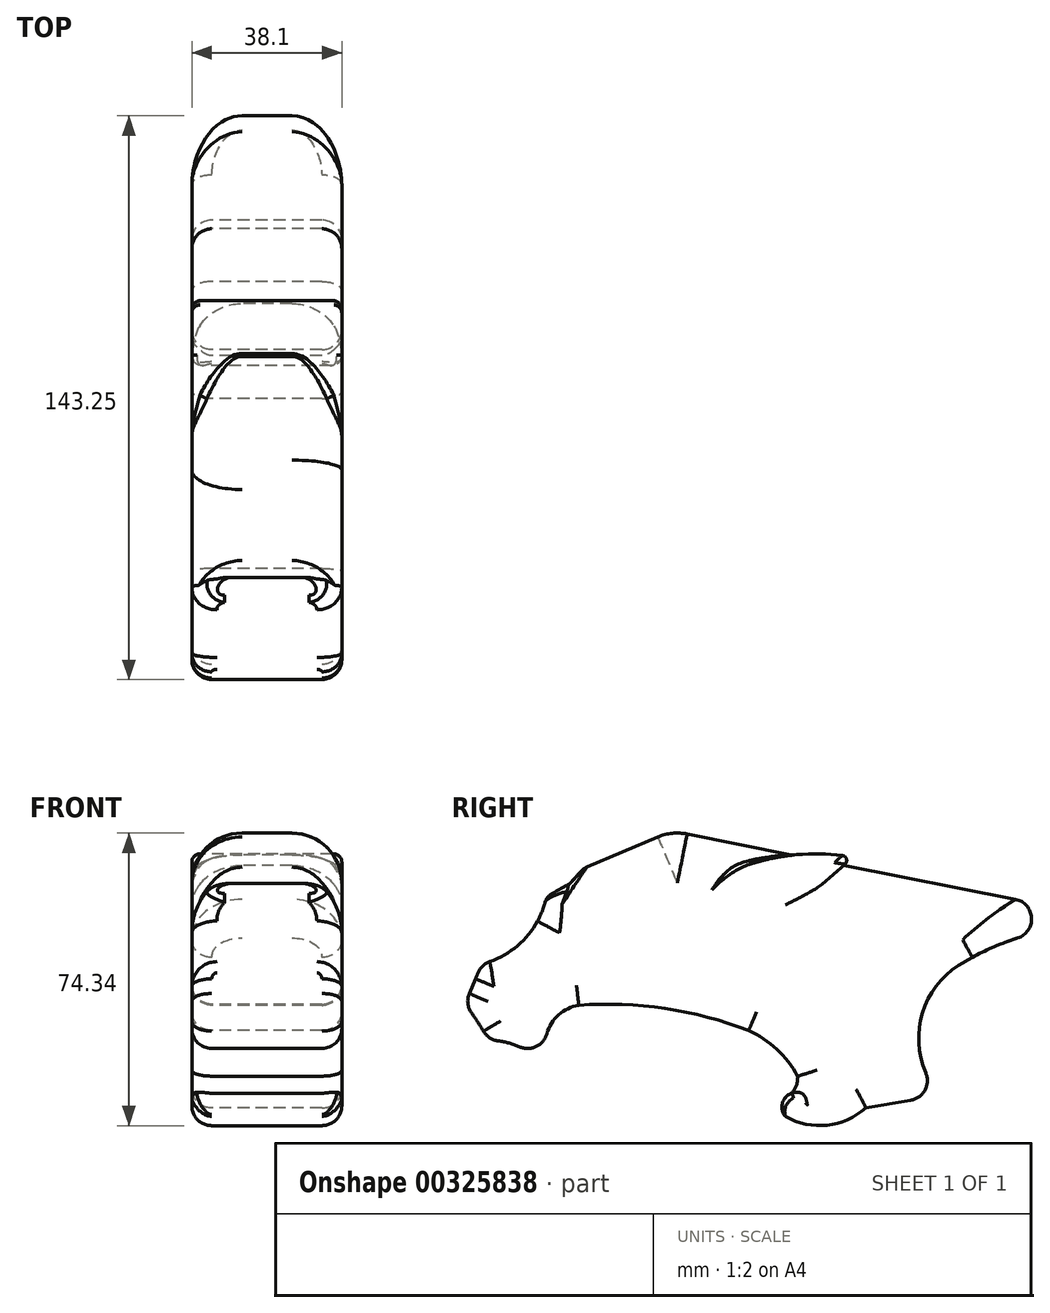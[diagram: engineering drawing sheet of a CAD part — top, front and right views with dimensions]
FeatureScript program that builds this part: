
annotation { "Feature Type Name" : "Feature", "Feature Type Description" : "" }
export const myFeature = defineFeature(function(context is Context, id is Id, definition is map)
    precondition{}
    {
        {
            var Q0;
            Q0=qCreatedBy(makeId("Right.planeOp"),FACE);
            var sketch = newSketch(context, id + "F0", { "sketchPlane" : qUnion([Q0])});
            skLineSegment(sketch, "E0", {"start": v(-74.7, -5.17) * mm, "end": v(-70.42, 5.02) * mm});
            skArc(sketch, "E1", {"start": v(-70.42, 5.02) * mm, "mid": v(-59.71, 11.2) * mm, "end": v(-53.98, 22.14) * mm});
            skLineSegment(sketch, "E2", {"start": v(-53.98, 22.14) * mm, "end": v(-48, 25.47) * mm});
            skLineSegment(sketch, "E3", {"start": v(-48, 25.47) * mm, "end": v(-44.48, 29.33) * mm});
            skLineSegment(sketch, "E4", {"start": v(-44.48, 29.33) * mm, "end": v(-22.06, 38.83) * mm});
            skLineSegment(sketch, "E5", {"start": v(-22.06, 38.83) * mm, "end": v(8.54, 32.7) * mm});
            skArc(sketch, "E6", {"start": v(23.98, 32.2) * mm, "mid": v(16.28, 33) * mm, "end": v(8.54, 32.7) * mm});
            skLineSegment(sketch, "E7", {"start": v(23.98, 32.2) * mm, "end": v(21.57, 30.12) * mm});
            skLineSegment(sketch, "E8", {"start": v(21.57, 30.12) * mm, "end": v(70.64, 20.4) * mm});
            skLineSegment(sketch, "E9", {"start": v(70.64, 20.4) * mm, "end": v(75.46, 13.94) * mm});
            skArc(sketch, "E10", {"start": v(75.46, 13.94) * mm, "mid": v(62.63, 10.57) * mm, "end": v(50.75, 4.69) * mm});
            skArc(sketch, "E11", {"start": v(50.75, 4.69) * mm, "mid": v(40.81, -10.74) * mm, "end": v(46.01, -28.34) * mm});
            skLineSegment(sketch, "E12", {"start": v(46.01, -28.34) * mm, "end": v(27.18, -31.52) * mm});
            skArc(sketch, "E13", {"start": v(6.53, -33.52) * mm, "mid": v(17.19, -35.96) * mm, "end": v(27.18, -31.52) * mm});
            skArc(sketch, "E14", {"start": v(8.33, -27.8) * mm, "mid": v(6.02, -30.21) * mm, "end": v(6.53, -33.52) * mm});
            skArc(sketch, "E15", {"start": v(8.33, -27.8) * mm, "mid": v(9.53, -25.78) * mm, "end": v(9.86, -23.46) * mm});
            skArc(sketch, "E16", {"start": v(9.86, -23.46) * mm, "mid": v(4.57, -16.65) * mm, "end": v(-2.6, -11.86) * mm});
            skArc(sketch, "E17", {"start": v(-2.6, -11.86) * mm, "mid": v(-23.82, -6.27) * mm, "end": v(-45.75, -5.45) * mm});
            skArc(sketch, "E18", {"start": v(-45.75, -5.45) * mm, "mid": v(-52.4, -9.61) * mm, "end": v(-54.05, -17.27) * mm});
            skLineSegment(sketch, "E19", {"start": v(-54.05, -17.27) * mm, "end": v(-58.43, -17.27) * mm});
            skArc(sketch, "E20", {"start": v(-58.43, -17.27) * mm, "mid": v(-63.35, -15.08) * mm, "end": v(-68.69, -14.36) * mm});
            skArc(sketch, "E21", {"start": v(-68.69, -14.36) * mm, "mid": v(-71.47, -9.62) * mm, "end": v(-74.7, -5.17) * mm});
            skSolve(sketch);
        }
        {
            var Q0;
            Q0 = qSketchRegion(id + "F0", true);
            extrude(context, id + "F1", {"entities" : qUnion([Q0]), "depth" : 19.05 * mm});
        }
        {
            var Q0;
            Q0=makeQuery(id+"F1.opExtrude","CAP_EDGE",EDGE,{"disambiguationData":[OSD([sQuery(id+"F0.wireOp",EDGE,"E8")])],"isStart":false});
            var Q1;
            Q1=makeQuery(id+"F1.opExtrude","CAP_EDGE",EDGE,{"disambiguationData":[OSD([sQuery(id+"F0.wireOp",EDGE,"E5")])],"isStart":false});
            fillet(context, id + "F2", {"entities" : qUnion([Q0, Q1]), "radius" : 12.7 * mm, "tangentPropagation" : true, "allowEdgeOverflow" : false});
        }
        {
            var Q0;
            Q0 = qSketchRegion(id + "F0", true);
            extrude(context, id + "F3", {"entities" : qUnion([Q0]), "operationType" : NewBodyOperationType.ADD, "depth" : -19.05 * mm});
        }
        {
            var Q0;
            Q0=makeQuery(id+"F3.opExtrude","CAP_EDGE",EDGE,{"disambiguationData":[OSD([sQuery(id+"F0.wireOp",EDGE,"E8")])],"isStart":false});
            fillet(context, id + "F4", {"entities" : qUnion([Q0]), "radius" : 12.7 * mm, "tangentPropagation" : true, "allowEdgeOverflow" : false});
        }
        {
            var Q0;
            Q0=makeQuery(id+"F3.opExtrude","CAP_EDGE",EDGE,{"disambiguationData":[OSD([sQuery(id+"F0.wireOp",EDGE,"E4")])],"isStart":false});
            fillet(context, id + "F5", {"entities" : qUnion([Q0]), "radius" : 12.7 * mm, "tangentPropagation" : true, "allowEdgeOverflow" : false});
        }
        {
            var Q0;
            Q0=makeQuery(id+"F3.opExtrude","CAP_EDGE",EDGE,{"disambiguationData":[OSD([sQuery(id+"F0.wireOp",EDGE,"E5")])],"isStart":false});
            fillet(context, id + "F6", {"entities" : qUnion([Q0]), "radius" : 12.7 * mm, "tangentPropagation" : true, "allowEdgeOverflow" : false});
        }
        {
            var Q0;
            Q0=makeQuery(id+"F3.opExtrude","CAP_EDGE",EDGE,{"disambiguationData":[OSD([sQuery(id+"F0.wireOp",EDGE,"E11")])],"isStart":false});
            fillet(context, id + "F7", {"entities" : qUnion([Q0]), "radius" : 5.08 * mm, "tangentPropagation" : true, "allowEdgeOverflow" : false});
        }
        {
            var Q0;
            Q0=makeQuery(id+"F3.opExtrude","CAP_EDGE",EDGE,{"disambiguationData":[OSD([sQuery(id+"F0.wireOp",EDGE,"E10")])],"isStart":false});
            fillet(context, id + "F8", {"entities" : qUnion([Q0]), "radius" : 5.08 * mm, "tangentPropagation" : true, "allowEdgeOverflow" : false});
        }
        {
            var Q0;
            Q0=makeQuery(id+"F1.opExtrude","CAP_EDGE",EDGE,{"disambiguationData":[OSD([sQuery(id+"F0.wireOp",EDGE,"E11")])],"isStart":false});
            fillet(context, id + "F9", {"entities" : qUnion([Q0]), "radius" : 5.08 * mm, "tangentPropagation" : true, "allowEdgeOverflow" : false});
        }
        {
            var Q0;
            Q0=makeQuery(id+"F1.opExtrude","CAP_EDGE",EDGE,{"disambiguationData":[OSD([sQuery(id+"F0.wireOp",EDGE,"E10")])],"isStart":false});
            fillet(context, id + "F10", {"entities" : qUnion([Q0]), "radius" : 5.08 * mm, "tangentPropagation" : true, "allowEdgeOverflow" : false});
        }
        {
            var Q0;
            {var subQ0=sQuery(id+"F0.wireOp",EDGE,"E12");var subQ1=sQuery(id+"F0.wireOp",EDGE,"E11");Q0=makeQuery(id+"F3.boolean.opBoolean","MERGE",EDGE,{"derivedFrom":[makeQuery(id+"F1.opExtrude","SWEPT_EDGE",EDGE,{"disambiguationData":[OSD([subQ1,subQ0])]}),makeQuery(id+"F3.opExtrude","SWEPT_EDGE",EDGE,{"disambiguationData":[OSD([subQ1,subQ0])]})]});}
            fillet(context, id + "F11", {"entities" : qUnion([Q0]), "radius" : 5.08 * mm, "tangentPropagation" : true, "allowEdgeOverflow" : false});
        }
        {
            var Q0;
            {var subQ0=sQuery(id+"F0.wireOp",EDGE,"E1");Q0=makeQuery(id+"F5.opFillet","BLEND_EDGE",EDGE,{"blendedFrom":[makeQuery(id+"F3.opExtrude","CAP_EDGE",EDGE,{"disambiguationData":[OSD([sQuery(id+"F0.wireOp",EDGE,"E4")])],"isStart":false}),makeQuery(id+"F3.boolean.opBoolean","MERGE",FACE,{"derivedFrom":[makeQuery(id+"F1.opExtrude","SWEPT_FACE",FACE,{"disambiguationData":[OSD([subQ0])]}),makeQuery(id+"F3.opExtrude","SWEPT_FACE",FACE,{"disambiguationData":[OSD([subQ0])]})]})],"blendedInto":[makeQuery(id+"F3.boolean.opBoolean","MERGE",FACE,{"derivedFrom":[makeQuery(id+"F1.opExtrude","SWEPT_FACE",FACE,{"disambiguationData":[OSD([subQ0])]}),makeQuery(id+"F3.opExtrude","SWEPT_FACE",FACE,{"disambiguationData":[OSD([subQ0])]})]})]});}
            fillet(context, id + "F12", {"entities" : qUnion([Q0]), "radius" : 6.35 * mm, "tangentPropagation" : true, "allowEdgeOverflow" : false});
        }
        {
            var Q0;
            {var subQ0=sQuery(id+"F0.wireOp",EDGE,"E1");Q0=makeQuery(id+"F6.opFillet","BLEND_EDGE",EDGE,{"blendedFrom":[makeQuery(id+"F1.opExtrude","CAP_EDGE",EDGE,{"disambiguationData":[OSD([sQuery(id+"F0.wireOp",EDGE,"E4")])],"isStart":false}),makeQuery(id+"F3.boolean.opBoolean","MERGE",FACE,{"derivedFrom":[makeQuery(id+"F1.opExtrude","SWEPT_FACE",FACE,{"disambiguationData":[OSD([subQ0])]}),makeQuery(id+"F3.opExtrude","SWEPT_FACE",FACE,{"disambiguationData":[OSD([subQ0])]})]})],"blendedInto":[makeQuery(id+"F3.boolean.opBoolean","MERGE",FACE,{"derivedFrom":[makeQuery(id+"F1.opExtrude","SWEPT_FACE",FACE,{"disambiguationData":[OSD([subQ0])]}),makeQuery(id+"F3.opExtrude","SWEPT_FACE",FACE,{"disambiguationData":[OSD([subQ0])]})]})]});}
            fillet(context, id + "F13", {"entities" : qUnion([Q0]), "radius" : 6.35 * mm, "tangentPropagation" : true, "allowEdgeOverflow" : false});
        }
        {
            var Q0;
            {var subQ0=sQuery(id+"F0.wireOp",EDGE,"E2");var subQ1=sQuery(id+"F0.wireOp",EDGE,"E1");Q0=makeQuery(id+"F3.boolean.opBoolean","MERGE",EDGE,{"derivedFrom":[makeQuery(id+"F1.opExtrude","SWEPT_EDGE",EDGE,{"disambiguationData":[OSD([subQ1,subQ0])]}),makeQuery(id+"F3.opExtrude","SWEPT_EDGE",EDGE,{"disambiguationData":[OSD([subQ1,subQ0])]})]});}
            fillet(context, id + "F14", {"entities" : qUnion([Q0]), "radius" : 3.8 * mm, "tangentPropagation" : true, "allowEdgeOverflow" : false});
        }
        {
            var Q0;
            {var subQ0=sQuery(id+"F0.wireOp",EDGE,"E3");Q0=makeQuery(id+"F5.opFillet","BLEND_EDGE",EDGE,{"blendedFrom":[makeQuery(id+"F3.opExtrude","CAP_EDGE",EDGE,{"disambiguationData":[OSD([sQuery(id+"F0.wireOp",EDGE,"E4")])],"isStart":false}),makeQuery(id+"F3.boolean.opBoolean","MERGE",FACE,{"derivedFrom":[makeQuery(id+"F1.opExtrude","SWEPT_FACE",FACE,{"disambiguationData":[OSD([subQ0])]}),makeQuery(id+"F3.opExtrude","SWEPT_FACE",FACE,{"disambiguationData":[OSD([subQ0])]})]})],"blendedInto":[makeQuery(id+"F3.boolean.opBoolean","MERGE",FACE,{"derivedFrom":[makeQuery(id+"F1.opExtrude","SWEPT_FACE",FACE,{"disambiguationData":[OSD([subQ0])]}),makeQuery(id+"F3.opExtrude","SWEPT_FACE",FACE,{"disambiguationData":[OSD([subQ0])]})]})]});}
            fillet(context, id + "F15", {"entities" : qUnion([Q0]), "radius" : 3.8 * mm, "tangentPropagation" : true, "allowEdgeOverflow" : false});
        }
        {
            var Q0;
            {var subQ0=sQuery(id+"F0.wireOp",EDGE,"E1");var subQ1=sQuery(id+"F0.wireOp",EDGE,"E0");Q0=makeQuery(id+"F3.boolean.opBoolean","MERGE",EDGE,{"derivedFrom":[makeQuery(id+"F1.opExtrude","SWEPT_EDGE",EDGE,{"disambiguationData":[OSD([subQ1,subQ0])]}),makeQuery(id+"F3.opExtrude","SWEPT_EDGE",EDGE,{"disambiguationData":[OSD([subQ1,subQ0])]})]});}
            fillet(context, id + "F16", {"entities" : qUnion([Q0]), "radius" : 5.08 * mm, "tangentPropagation" : true, "allowEdgeOverflow" : false});
        }
        {
            var Q0;
            {var subQ0=sQuery(id+"F0.wireOp",EDGE,"E21");var subQ1=sQuery(id+"F0.wireOp",EDGE,"E0");Q0=makeQuery(id+"F3.boolean.opBoolean","MERGE",EDGE,{"derivedFrom":[makeQuery(id+"F1.opExtrude","SWEPT_EDGE",EDGE,{"disambiguationData":[OSD([subQ1,subQ0])]}),makeQuery(id+"F3.opExtrude","SWEPT_EDGE",EDGE,{"disambiguationData":[OSD([subQ1,subQ0])]})]});}
            fillet(context, id + "F17", {"entities" : qUnion([Q0]), "radius" : 5.08 * mm, "tangentPropagation" : true, "allowEdgeOverflow" : false});
        }
        {
            var Q0;
            {var subQ0=sQuery(id+"F0.wireOp",EDGE,"E21");var subQ1=sQuery(id+"F0.wireOp",EDGE,"E20");Q0=makeQuery(id+"F3.boolean.opBoolean","MERGE",EDGE,{"derivedFrom":[makeQuery(id+"F1.opExtrude","SWEPT_EDGE",EDGE,{"disambiguationData":[OSD([subQ1,subQ0])]}),makeQuery(id+"F3.opExtrude","SWEPT_EDGE",EDGE,{"disambiguationData":[OSD([subQ1,subQ0])]})]});}
            fillet(context, id + "F18", {"entities" : qUnion([Q0]), "radius" : 5.08 * mm, "tangentPropagation" : true, "allowEdgeOverflow" : false});
        }
        {
            var Q0;
            {var subQ0=sQuery(id+"F0.wireOp",EDGE,"E19");var subQ1=sQuery(id+"F0.wireOp",EDGE,"E18");Q0=makeQuery(id+"F3.boolean.opBoolean","MERGE",EDGE,{"derivedFrom":[makeQuery(id+"F1.opExtrude","SWEPT_EDGE",EDGE,{"disambiguationData":[OSD([subQ1,subQ0])]}),makeQuery(id+"F3.opExtrude","SWEPT_EDGE",EDGE,{"disambiguationData":[OSD([subQ1,subQ0])]})]});}
            fillet(context, id + "F19", {"entities" : qUnion([Q0]), "radius" : 2.54 * mm, "tangentPropagation" : true, "allowEdgeOverflow" : false});
        }
        {
            var Q0;
            {var subQ0=sQuery(id+"F0.wireOp",EDGE,"E7");var subQ1=sQuery(id+"F0.wireOp",EDGE,"E6");Q0=makeQuery(id+"F3.boolean.opBoolean","MERGE",EDGE,{"derivedFrom":[makeQuery(id+"F1.opExtrude","SWEPT_EDGE",EDGE,{"disambiguationData":[OSD([subQ1,subQ0])]}),makeQuery(id+"F3.opExtrude","SWEPT_EDGE",EDGE,{"disambiguationData":[OSD([subQ1,subQ0])]})]});}
            fillet(context, id + "F20", {"entities" : qUnion([Q0]), "radius" : 1.27 * mm, "tangentPropagation" : true, "allowEdgeOverflow" : false});
        }
        {
            var Q0;
            Q0=makeQuery(id+"F1.opExtrude","CAP_EDGE",EDGE,{"disambiguationData":[OSD([sQuery(id+"F0.wireOp",EDGE,"E13")])],"isStart":false});
            fillet(context, id + "F21", {"entities" : qUnion([Q0]), "radius" : 5.08 * mm, "tangentPropagation" : true, "allowEdgeOverflow" : false});
        }
        {
            var Q0;
            Q0=makeQuery(id+"F3.opExtrude","CAP_EDGE",EDGE,{"disambiguationData":[OSD([sQuery(id+"F0.wireOp",EDGE,"E13")])],"isStart":false});
            fillet(context, id + "F22", {"entities" : qUnion([Q0]), "radius" : 5.08 * mm, "tangentPropagation" : true, "allowEdgeOverflow" : false});
        }
        {
            var Q0;
            Q0=makeQuery(id+"F3.opExtrude","CAP_EDGE",EDGE,{"disambiguationData":[OSD([sQuery(id+"F0.wireOp",EDGE,"E16")])],"isStart":false});
            var Q1;
            Q1=makeQuery(id+"F3.opExtrude","CAP_EDGE",EDGE,{"disambiguationData":[OSD([sQuery(id+"F0.wireOp",EDGE,"E17")])],"isStart":false});
            var Q2;
            Q2=makeQuery(id+"F3.opExtrude","CAP_EDGE",EDGE,{"disambiguationData":[OSD([sQuery(id+"F0.wireOp",EDGE,"E18")])],"isStart":false});
            var Q3;
            Q3=makeQuery(id+"F3.opExtrude","CAP_EDGE",EDGE,{"disambiguationData":[OSD([sQuery(id+"F0.wireOp",EDGE,"E15")])],"isStart":false});
            fillet(context, id + "F23", {"entities" : qUnion([Q0, Q1, Q2, Q3]), "radius" : 5.08 * mm, "tangentPropagation" : true, "allowEdgeOverflow" : false});
        }
        {
            var Q0;
            Q0=makeQuery(id+"F1.opExtrude","CAP_EDGE",EDGE,{"disambiguationData":[OSD([sQuery(id+"F0.wireOp",EDGE,"E17")])],"isStart":false});
            var Q1;
            Q1=makeQuery(id+"F1.opExtrude","CAP_EDGE",EDGE,{"disambiguationData":[OSD([sQuery(id+"F0.wireOp",EDGE,"E16")])],"isStart":false});
            var Q2;
            Q2=makeQuery(id+"F1.opExtrude","CAP_EDGE",EDGE,{"disambiguationData":[OSD([sQuery(id+"F0.wireOp",EDGE,"E15")])],"isStart":false});
            fillet(context, id + "F24", {"entities" : qUnion([Q0, Q1, Q2]), "radius" : 5.08 * mm, "tangentPropagation" : true, "allowEdgeOverflow" : false});
        }
        {
            var Q0;
            {var subQ0=sQuery(id+"F0.wireOp",EDGE,"E14");Q0=makeQuery(id+"F22.opFillet","BLEND_EDGE",EDGE,{"blendedFrom":[makeQuery(id+"F3.opExtrude","CAP_EDGE",EDGE,{"disambiguationData":[OSD([sQuery(id+"F0.wireOp",EDGE,"E13")])],"isStart":false}),makeQuery(id+"F3.boolean.opBoolean","MERGE",FACE,{"derivedFrom":[makeQuery(id+"F1.opExtrude","SWEPT_FACE",FACE,{"disambiguationData":[OSD([subQ0])]}),makeQuery(id+"F3.opExtrude","SWEPT_FACE",FACE,{"disambiguationData":[OSD([subQ0])]})]})],"blendedInto":[makeQuery(id+"F3.boolean.opBoolean","MERGE",FACE,{"derivedFrom":[makeQuery(id+"F1.opExtrude","SWEPT_FACE",FACE,{"disambiguationData":[OSD([subQ0])]}),makeQuery(id+"F3.opExtrude","SWEPT_FACE",FACE,{"disambiguationData":[OSD([subQ0])]})]})]});}
            var Q1;
            Q1=makeQuery(id+"F3.opExtrude","CAP_EDGE",EDGE,{"disambiguationData":[OSD([sQuery(id+"F0.wireOp",EDGE,"E14")])],"isStart":false});
            fillet(context, id + "F25", {"entities" : qUnion([Q0, Q1]), "radius" : 1.27 * mm, "tangentPropagation" : true, "allowEdgeOverflow" : false});
        }
        {
            var Q0;
            Q0=makeQuery(id+"F1.opExtrude","CAP_EDGE",EDGE,{"disambiguationData":[OSD([sQuery(id+"F0.wireOp",EDGE,"E6")])],"isStart":false});
            fillet(context, id + "F26", {"entities" : qUnion([Q0]), "radius" : 2.03 * mm, "tangentPropagation" : true, "allowEdgeOverflow" : false});
        }
        {
            var Q0;
            Q0=makeQuery(id+"F3.opExtrude","CAP_EDGE",EDGE,{"disambiguationData":[OSD([sQuery(id+"F0.wireOp",EDGE,"E6")])],"isStart":false});
            fillet(context, id + "F27", {"entities" : qUnion([Q0]), "radius" : 2.03 * mm, "tangentPropagation" : true, "allowEdgeOverflow" : false});
        }
        {
            var Q0;
            {var subQ0=sQuery(id+"F0.wireOp",EDGE,"E6");Q0=makeQuery(id+"F3.boolean.opBoolean","MERGE",FACE,{"derivedFrom":[makeQuery(id+"F1.opExtrude","SWEPT_FACE",FACE,{"disambiguationData":[OSD([subQ0])]}),makeQuery(id+"F3.opExtrude","SWEPT_FACE",FACE,{"disambiguationData":[OSD([subQ0])]})]});}
            chamfer(context, id + "F28", {"entities" : qUnion([Q0]), "width" : 2.54 * mm, "tangentPropagation" : true});
        }
    });
